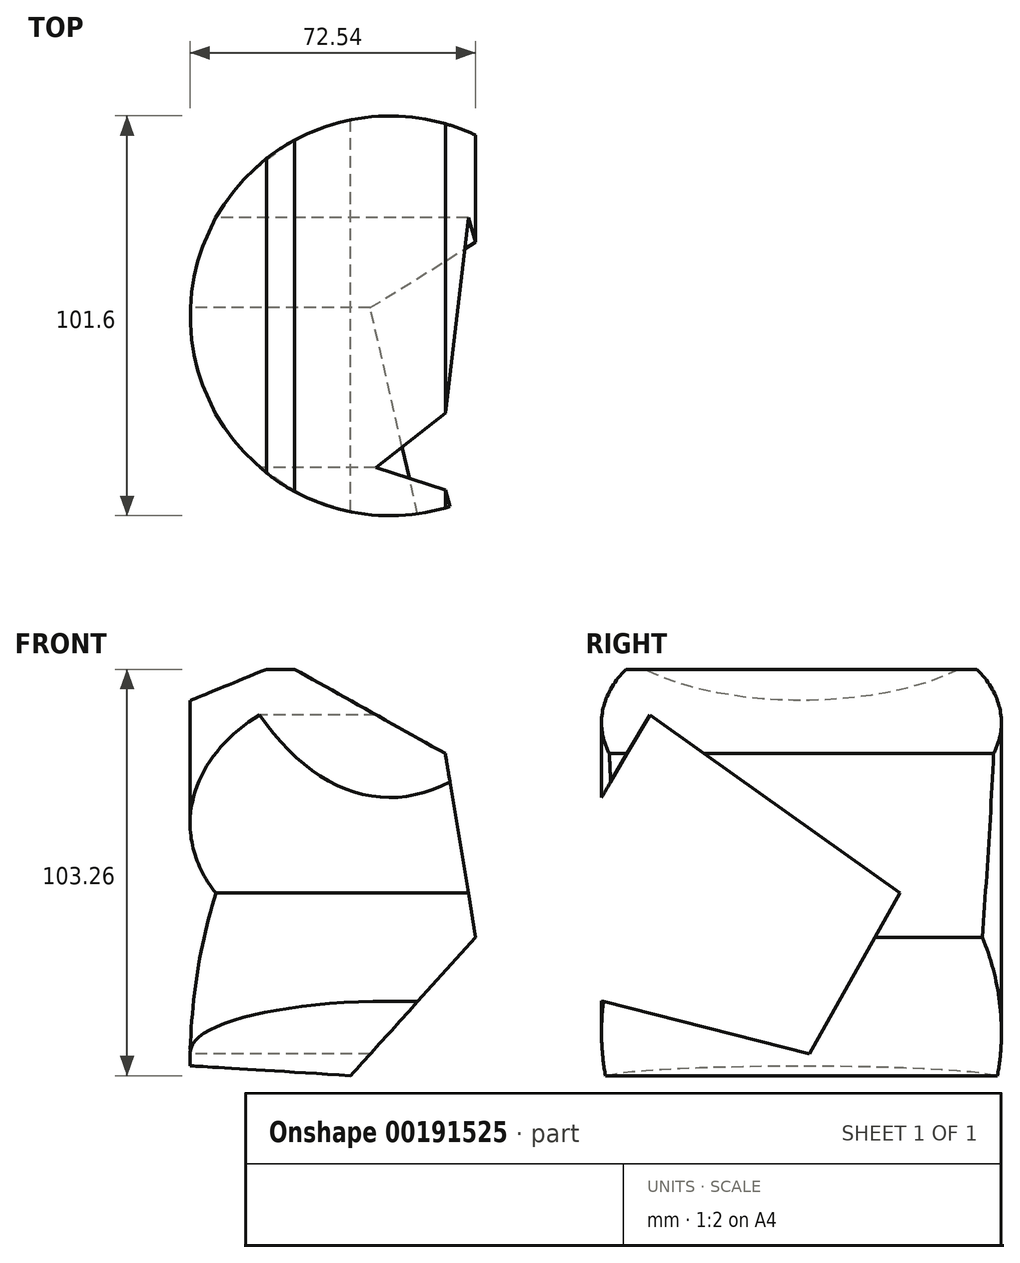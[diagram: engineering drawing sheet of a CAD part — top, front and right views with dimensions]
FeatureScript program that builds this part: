
annotation { "Feature Type Name" : "Feature", "Feature Type Description" : "" }
export const myFeature = defineFeature(function(context is Context, id is Id, definition is map)
    precondition{}
    {
        {
            var Q0;
            Q0=qCreatedBy(makeId("Top.planeOp"),FACE);
            var sketch = newSketch(context, id + "F0", { "sketchPlane" : qUnion([Q0])});
            skCircle(sketch, "E0", {"center": v(0, 0) * mm, "radius": 50.8 * mm});
            skSolve(sketch);
        }
        {
            var Q0;
            Q0 = qSketchRegion(id + "F0", true);
            extrude(context, id + "F1", {"entities" : qUnion([Q0]), "endBound" : BoundingType.SYMMETRIC, "depth" : 127 * mm});
        }
        {
            var Q0;
            Q0=qCreatedBy(makeId("Front.planeOp"),FACE);
            var sketch = newSketch(context, id + "F2", { "sketchPlane" : qUnion([Q0])});
            skCircle(sketch, "E1.cCircle", {"center": v(-30.58, 10.73) * mm, "radius": 49.13 * mm, "construction": true});
            skLineSegment(sketch, "E1.0", {"start": v(21.74, -4.64) * mm, "end": v(-9.98, -39.76) * mm});
            skLineSegment(sketch, "E1.1", {"start": v(-9.98, -39.76) * mm, "end": v(-57.21, -36.86) * mm});
            skLineSegment(sketch, "E1.2", {"start": v(-57.21, -36.86) * mm, "end": v(-84.4, 1.88) * mm});
            skLineSegment(sketch, "E1.3", {"start": v(-84.4, 1.88) * mm, "end": v(-71.05, 47.29) * mm});
            skLineSegment(sketch, "E1.4", {"start": v(-71.05, 47.29) * mm, "end": v(-27.23, 65.16) * mm});
            skLineSegment(sketch, "E1.5", {"start": v(-27.23, 65.16) * mm, "end": v(14.06, 42.05) * mm});
            skLineSegment(sketch, "E1.6", {"start": v(14.06, 42.05) * mm, "end": v(21.74, -4.64) * mm});
            skSolve(sketch);
        }
        {
            var Q0;
            Q0 = qSketchRegion(id + "F2", true);
            extrude(context, id + "F3", {"entities" : qUnion([Q0]), "operationType" : NewBodyOperationType.INTERSECT, "endBound" : BoundingType.SYMMETRIC, "depth" : 152.4 * mm});
        }
        {
            var Q0;
            Q0=qCreatedBy(makeId("Right.planeOp"),FACE);
            var sketch = newSketch(context, id + "F4", { "sketchPlane" : qUnion([Q0])});
            skLineSegment(sketch, "E2", {"start": v(-59.98, 15.14) * mm, "end": v(-38.52, 51.9) * mm});
            skLineSegment(sketch, "E3", {"start": v(-38.52, 51.9) * mm, "end": v(25, 6.62) * mm});
            skLineSegment(sketch, "E4", {"start": v(25, 6.62) * mm, "end": v(2.06, -34.26) * mm});
            skLineSegment(sketch, "E5", {"start": v(2.06, -34.26) * mm, "end": v(-67.34, -16.61) * mm});
            skLineSegment(sketch, "E6", {"start": v(-67.34, -16.61) * mm, "end": v(-59.98, 15.14) * mm});
            skSolve(sketch);
        }
        {
            var Q0;
            Q0 = qSketchRegion(id + "F4", true);
            extrude(context, id + "F5", {"entities" : qUnion([Q0]), "operationType" : NewBodyOperationType.REMOVE, "endBound" : BoundingType.SYMMETRIC, "depth" : 152.4 * mm});
        }
    });
